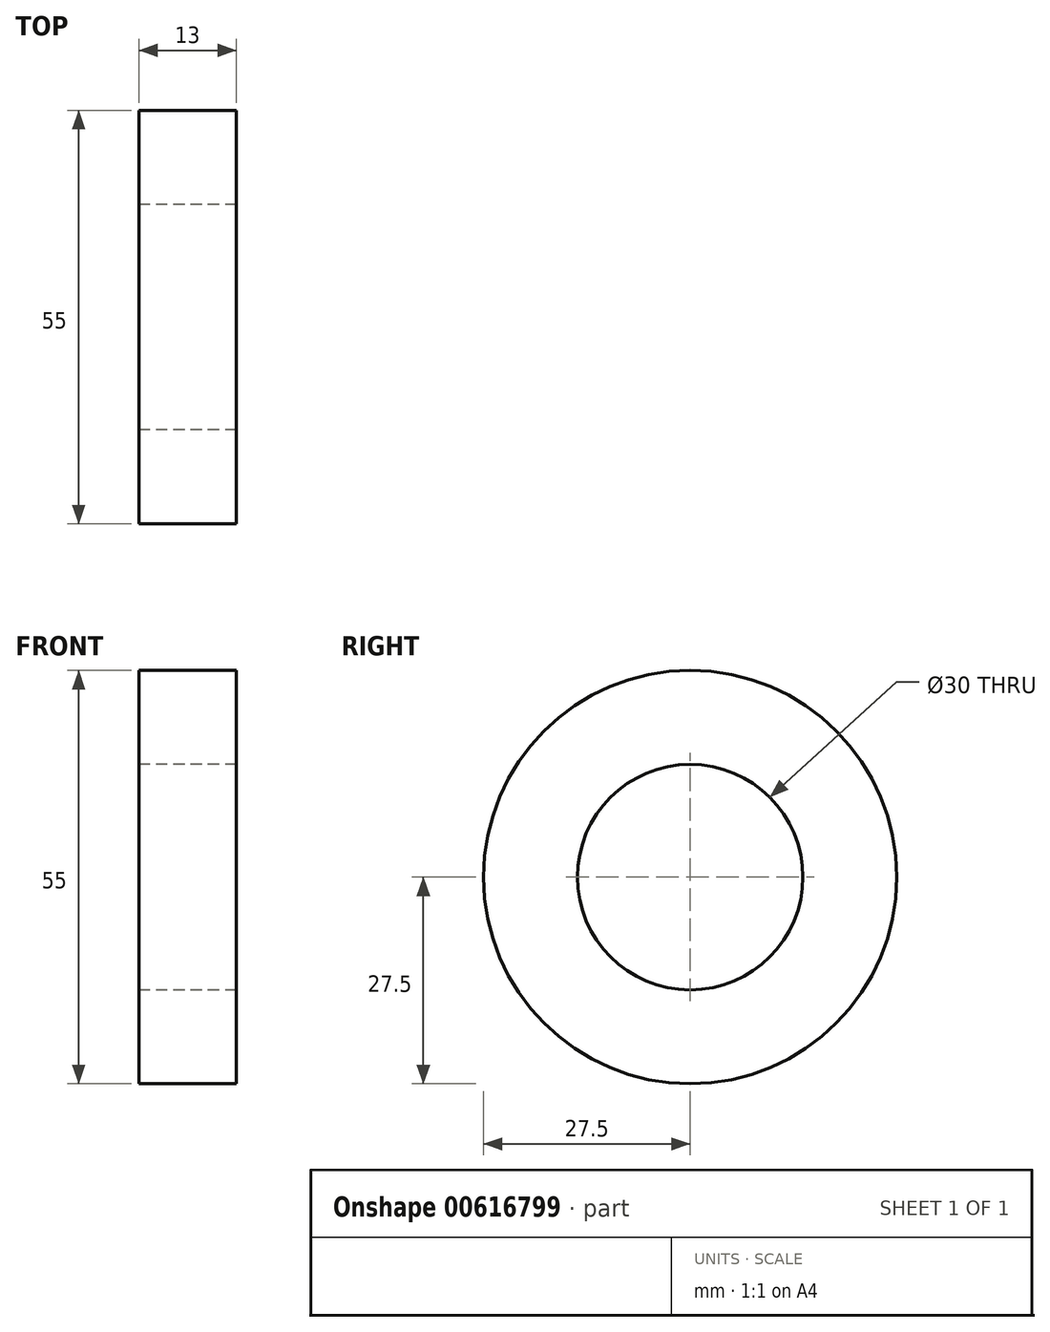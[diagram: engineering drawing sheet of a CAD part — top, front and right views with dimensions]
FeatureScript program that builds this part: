
annotation { "Feature Type Name" : "Feature", "Feature Type Description" : "" }
export const myFeature = defineFeature(function(context is Context, id is Id, definition is map)
    precondition{}
    {
        {
            var Q0;
            Q0=qCreatedBy(makeId("Right.planeOp"),FACE);
            var sketch = newSketch(context, id + "F0", { "sketchPlane" : qUnion([Q0])});
            skCircle(sketch, "E0", {"center": v(0, 0) * mm, "radius": 15 * mm});
            skCircle(sketch, "E1", {"center": v(0, 0) * mm, "radius": 27.5 * mm});
            skSolve(sketch);
        }
        {
            var Q0;
            Q0 = qSketchRegion(id + "F0", true);
            extrude(context, id + "F1", {"entities" : qUnion([Q0]), "depth" : 13 * mm, "offsetDistance" : 25 * mm});
        }
    });
